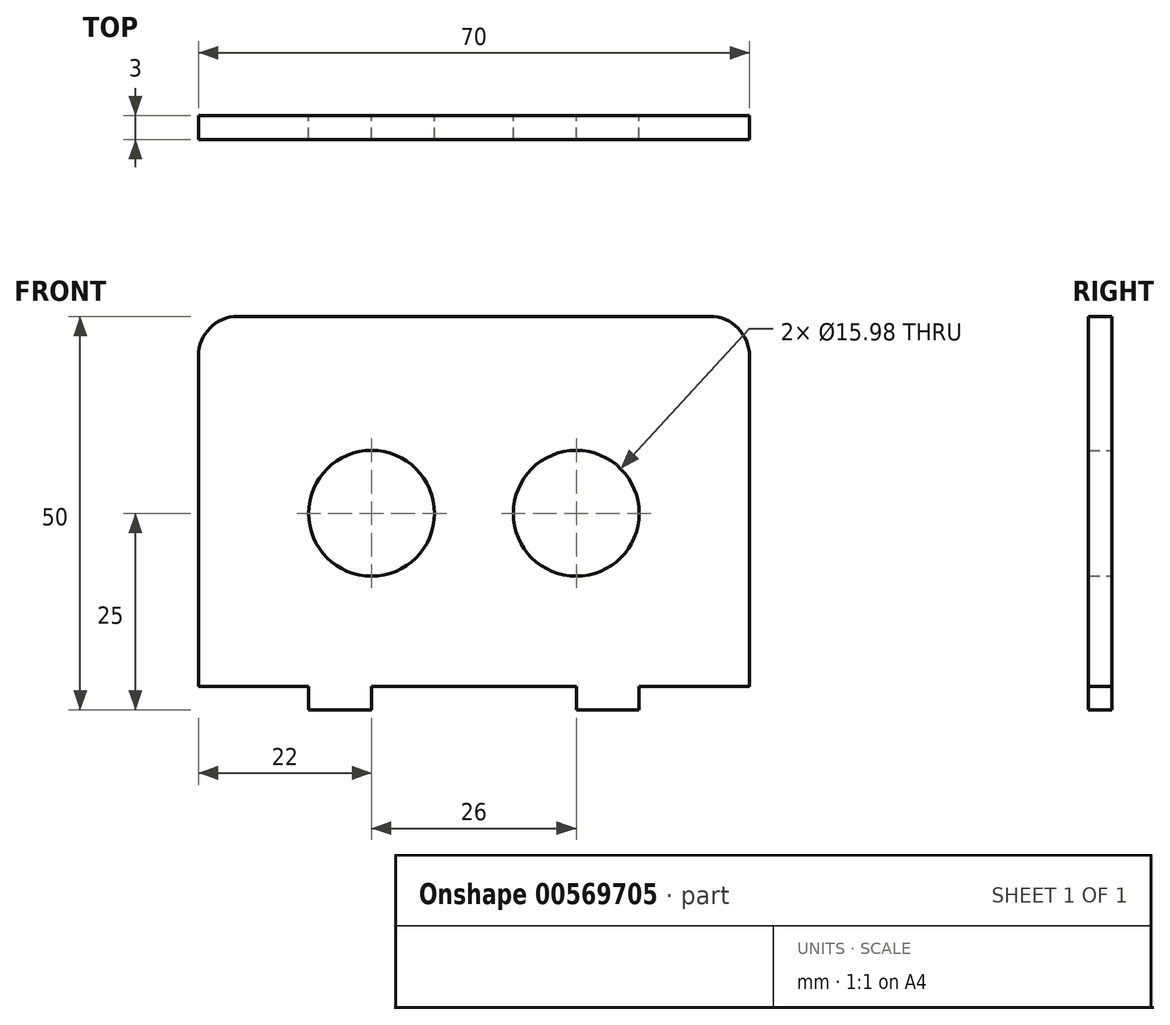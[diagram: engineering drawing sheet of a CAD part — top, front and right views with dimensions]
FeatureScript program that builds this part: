
annotation { "Feature Type Name" : "Feature", "Feature Type Description" : "" }
export const myFeature = defineFeature(function(context is Context, id is Id, definition is map)
    precondition{}
    {
        {
            var Q0;
            Q0=qCreatedBy(makeId("Front.planeOp"),FACE);
            var sketch = newSketch(context, id + "F0", { "sketchPlane" : qUnion([Q0])});
            skLineSegment(sketch, "E0", {"start": v(-30, 25) * mm, "end": v(30, 25) * mm});
            skLineSegment(sketch, "E1", {"start": v(35, 20) * mm, "end": v(35, -22) * mm});
            skLineSegment(sketch, "E2", {"start": v(-35, 20) * mm, "end": v(-35, -22) * mm});
            skLineSegment(sketch, "E3", {"start": v(-21, -25) * mm, "end": v(-13, -25) * mm});
            skCircle(sketch, "E4", {"center": v(-13, 0) * mm, "radius": 8 * mm});
            skCircle(sketch, "E5", {"center": v(13, 0) * mm, "radius": 8 * mm});
            skLineSegment(sketch, "E6", {"start": v(-50.38, -22) * mm, "end": v(-21, -22) * mm, "construction": true});
            skLineSegment(sketch, "E7", {"start": v(-21, -25) * mm, "end": v(-21, -22) * mm});
            skLineSegment(sketch, "E8", {"start": v(-13, -22) * mm, "end": v(-13, -25) * mm});
            skLineSegment(sketch, "E9.trimOffspring", {"start": v(-13, -22) * mm, "end": v(44.63, -22) * mm, "construction": true});
            skPoint(sketch, "E10.orphan", {"position": v(-35, -25) * mm});
            skLineSegment(sketch, "E11", {"start": v(13, -22) * mm, "end": v(13, -25) * mm});
            skLineSegment(sketch, "E12", {"start": v(13, -25) * mm, "end": v(21, -25) * mm});
            skLineSegment(sketch, "E13", {"start": v(21, -25) * mm, "end": v(21, -22) * mm});
            skLineSegment(sketch, "E14", {"start": v(-35, -22) * mm, "end": v(-21, -22) * mm});
            skLineSegment(sketch, "E15", {"start": v(-13, -22) * mm, "end": v(13, -22) * mm});
            skLineSegment(sketch, "E16", {"start": v(21, -22) * mm, "end": v(35, -22) * mm});
            skPoint(sketch, "E17.orphan", {"position": v(35, -25) * mm});
            skPoint(sketch, "E18.visualSharp", {"position": v(-35, 25) * mm});
            skArc(sketch, "E18.filletArc", {"start": v(-30, 25) * mm, "mid": v(-33.54, 23.54) * mm, "end": v(-35, 20) * mm});
            skPoint(sketch, "E19.visualSharp", {"position": v(35, 25) * mm});
            skArc(sketch, "E19.filletArc", {"start": v(35, 20) * mm, "mid": v(33.54, 23.54) * mm, "end": v(30, 25) * mm});
            skSolve(sketch);
        }
        {
            var Q0;
            Q0 = qSketchRegion(id + "F0", true);
            extrude(context, id + "F1", {"entities" : qUnion([Q0]), "depth" : 3 * mm, "offsetDistance" : 25 * mm});
        }
    });
